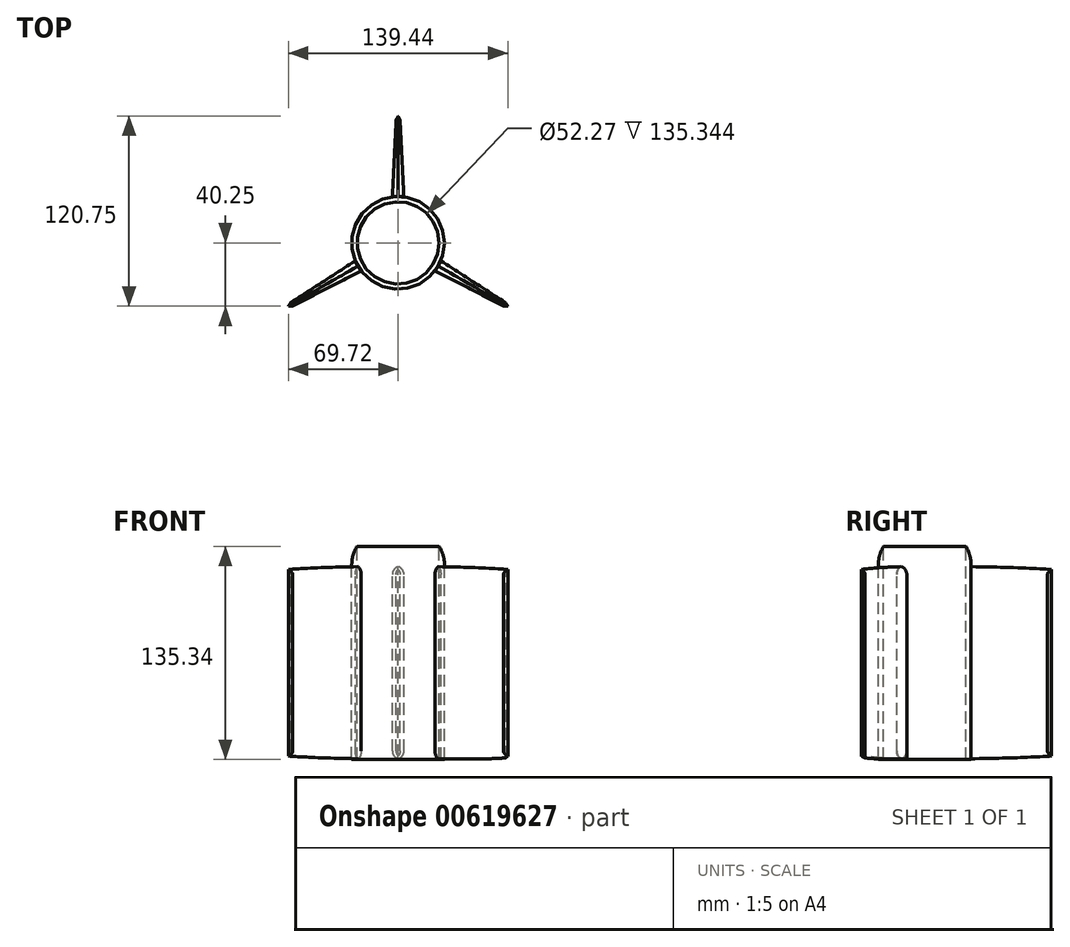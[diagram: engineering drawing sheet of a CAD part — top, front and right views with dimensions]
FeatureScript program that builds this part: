
annotation { "Feature Type Name" : "Feature", "Feature Type Description" : "" }
export const myFeature = defineFeature(function(context is Context, id is Id, definition is map)
    precondition{}
    {
        {
            var Q0;
            Q0=qCreatedBy(makeId("Front.planeOp"),FACE);
            var sketch = newSketch(context, id + "F0", { "sketchPlane" : qUnion([Q0])});
            skLineSegment(sketch, "E0.bottom", {"start": v(-26.13, 61.32) * mm, "end": v(26.13, 61.32) * mm});
            skLineSegment(sketch, "E0.top", {"start": v(-26.13, -61.32) * mm, "end": v(26.13, -61.32) * mm});
            skLineSegment(sketch, "E0.left", {"start": v(-26.13, 61.32) * mm, "end": v(-26.13, -61.32) * mm});
            skLineSegment(sketch, "E0.right", {"start": v(26.13, 61.32) * mm, "end": v(26.13, -61.32) * mm});
            skPoint(sketch, "E0.middle", {"position": v(0, 0) * mm});
            skLineSegment(sketch, "E1", {"start": v(0, 61.32) * mm, "end": v(0, -61.32) * mm});
            skLineSegment(sketch, "E2.bottom", {"start": v(-29.43, 61.32) * mm, "end": v(29.43, 61.32) * mm});
            skLineSegment(sketch, "E2.top", {"start": v(-29.43, -61.32) * mm, "end": v(29.43, -61.32) * mm});
            skLineSegment(sketch, "E2.left", {"start": v(-29.43, 61.32) * mm, "end": v(-29.43, -61.32) * mm});
            skLineSegment(sketch, "E2.right", {"start": v(29.43, 61.32) * mm, "end": v(29.43, -61.32) * mm});
            skSolve(sketch);
        }
        {
            var Q0;
            {var subQ0=sQuery(id+"F0.wireOp",EDGE,"E0.left");Q0=makeQuery(id+"F0.imprint","IMPRINT",FACE,{"disambiguationData":[TD([[makeQuery(id+"F0.imprint","IMPRINT",EDGE,{"derivedFrom":subQ0}),-1.0]])]});}
            var Q1;
            Q1=sQuery(id+"F0.wireOp",EDGE,"E1");
            revolve(context, id + "F1", {"entities" : qUnion([Q0]), "axis" : qUnion([Q1]), "revolveType" : RevolveType.FULL});
        }
        {
            var Q0;
            Q0=makeQuery(id+"F1.opRevolve","SWEPT_FACE",FACE,{"disambiguationData":[OSD([sQuery(id+"F0.wireOp",EDGE,"E2.bottom")])]});
            var sketch = newSketch(context, id + "F2", { "sketchPlane" : qUnion([Q0])});
            skLineSegment(sketch, "E3", {"start": v(0, 29.43) * mm, "end": v(0, 80.5) * mm});
            skCircle(sketch, "E4.cCircle", {"center": v(0, 0) * mm, "radius": 29.43 * mm, "construction": true});
            skLineSegment(sketch, "E5.1.0", {"start": v(-25.49, -14.72) * mm, "end": v(-69.72, -40.25) * mm});
            skLineSegment(sketch, "E5.2.0", {"start": v(25.49, -14.72) * mm, "end": v(69.72, -40.25) * mm});
            skLineSegment(sketch, "E6", {"start": v(3.68, 29.2) * mm, "end": v(1.25, 78.03) * mm});
            skLineSegment(sketch, "E7", {"start": v(1.25, 78.03) * mm, "end": v(0, 80.5) * mm});
            skLineSegment(sketch, "E8.MirrorCS", {"start": v(-3.68, 29.2) * mm, "end": v(-1.25, 78.03) * mm});
            skLineSegment(sketch, "E9.MirrorCS", {"start": v(-1.25, 78.03) * mm, "end": v(0, 80.5) * mm});
            skLineSegment(sketch, "E10.1.0", {"start": v(-27.13, -11.41) * mm, "end": v(-68.2, -37.93) * mm});
            skLineSegment(sketch, "E10.2.0", {"start": v(23.45, -17.79) * mm, "end": v(66.95, -40.1) * mm});
            skLineSegment(sketch, "E11.1.0", {"start": v(-23.45, -17.79) * mm, "end": v(-66.95, -40.1) * mm});
            skLineSegment(sketch, "E11.2.0", {"start": v(27.13, -11.41) * mm, "end": v(68.2, -37.93) * mm});
            skLineSegment(sketch, "E12.1.0", {"start": v(-68.2, -37.93) * mm, "end": v(-69.72, -40.25) * mm});
            skLineSegment(sketch, "E12.1.1", {"start": v(-66.95, -40.1) * mm, "end": v(-69.72, -40.25) * mm});
            skLineSegment(sketch, "E12.2.0", {"start": v(66.95, -40.1) * mm, "end": v(69.72, -40.25) * mm});
            skLineSegment(sketch, "E12.2.1", {"start": v(68.2, -37.93) * mm, "end": v(69.72, -40.25) * mm});
            skSolve(sketch);
        }
        {
            var Q0;
            {var subQ0=sQuery(id+"F2.wireOp",EDGE,"E3");Q0=makeQuery(id+"F2.imprint","IMPRINT",FACE,{"disambiguationData":[TD([[makeQuery(id+"F2.imprint","IMPRINT",EDGE,{"derivedFrom":subQ0}),-1.0]])]});}
            var Q1;
            {var subQ0=sQuery(id+"F2.wireOp",EDGE,"E3");Q1=makeQuery(id+"F2.imprint","IMPRINT",FACE,{"disambiguationData":[TD([[makeQuery(id+"F2.imprint","IMPRINT",EDGE,{"derivedFrom":subQ0}),1.0]])]});}
            var Q2;
            {var subQ0=sQuery(id+"F2.wireOp",EDGE,"E5.1.0");Q2=makeQuery(id+"F2.imprint","IMPRINT",FACE,{"disambiguationData":[TD([[makeQuery(id+"F2.imprint","IMPRINT",EDGE,{"derivedFrom":subQ0}),-1.0]])]});}
            var Q3;
            {var subQ0=sQuery(id+"F2.wireOp",EDGE,"E5.1.0");Q3=makeQuery(id+"F2.imprint","IMPRINT",FACE,{"disambiguationData":[TD([[makeQuery(id+"F2.imprint","IMPRINT",EDGE,{"derivedFrom":subQ0}),1.0]])]});}
            var Q4;
            {var subQ0=sQuery(id+"F2.wireOp",EDGE,"E5.2.0");Q4=makeQuery(id+"F2.imprint","IMPRINT",FACE,{"disambiguationData":[TD([[makeQuery(id+"F2.imprint","IMPRINT",EDGE,{"derivedFrom":subQ0}),-1.0]])]});}
            var Q5;
            {var subQ0=sQuery(id+"F2.wireOp",EDGE,"E5.2.0");Q5=makeQuery(id+"F2.imprint","IMPRINT",FACE,{"disambiguationData":[TD([[makeQuery(id+"F2.imprint","IMPRINT",EDGE,{"derivedFrom":subQ0}),1.0]])]});}
            extrude(context, id + "F3", {"entities" : qUnion([Q0, Q1, Q2, Q3, Q4, Q5]), "oppositeDirection" : true, "depth" : 122.43 * mm, "offsetDistance" : 25.4 * mm});
        }
        {
            var Q0;
            Q0=makeQuery(id+"F3.opExtrude","CAP_EDGE",EDGE,{"disambiguationData":[OSD([sQuery(id+"F2.wireOp",EDGE,"E8.MirrorCS")])],"isStart":true});
            var Q1;
            Q1=makeQuery(id+"F3.opExtrude","CAP_EDGE",EDGE,{"disambiguationData":[OSD([sQuery(id+"F2.wireOp",EDGE,"E11.1.0")])],"isStart":true});
            var Q2;
            Q2=makeQuery(id+"F3.opExtrude","CAP_EDGE",EDGE,{"disambiguationData":[OSD([sQuery(id+"F2.wireOp",EDGE,"E11.2.0")])],"isStart":true});
            var Q3;
            Q3=makeQuery(id+"F3.opExtrude","CAP_EDGE",EDGE,{"disambiguationData":[OSD([sQuery(id+"F2.wireOp",EDGE,"E10.1.0")])],"isStart":true});
            var Q4;
            Q4=makeQuery(id+"F3.opExtrude","CAP_EDGE",EDGE,{"disambiguationData":[OSD([sQuery(id+"F2.wireOp",EDGE,"E6")])],"isStart":true});
            var Q5;
            Q5=makeQuery(id+"F3.opExtrude","CAP_EDGE",EDGE,{"disambiguationData":[OSD([sQuery(id+"F2.wireOp",EDGE,"E10.2.0")])],"isStart":true});
            fillet(context, id + "F4", {"entities" : qUnion([Q0, Q1, Q2, Q3, Q4, Q5]), "radius" : 5.08 * mm, "tangentPropagation" : true, "rho" : .4, "crossSection" : FilletCrossSection.CONIC, "allowEdgeOverflow" : false});
        }
        {
            var Q0;
            Q0=makeQuery(id+"F3.opExtrude","CAP_EDGE",EDGE,{"disambiguationData":[OSD([sQuery(id+"F2.wireOp",EDGE,"E10.2.0")])],"isStart":false});
            var Q1;
            Q1=makeQuery(id+"F3.opExtrude","CAP_EDGE",EDGE,{"disambiguationData":[OSD([sQuery(id+"F2.wireOp",EDGE,"E8.MirrorCS")])],"isStart":false});
            var Q2;
            Q2=makeQuery(id+"F3.opExtrude","CAP_EDGE",EDGE,{"disambiguationData":[OSD([sQuery(id+"F2.wireOp",EDGE,"E6")])],"isStart":false});
            var Q3;
            Q3=makeQuery(id+"F3.opExtrude","CAP_EDGE",EDGE,{"disambiguationData":[OSD([sQuery(id+"F2.wireOp",EDGE,"E10.1.0")])],"isStart":false});
            var Q4;
            Q4=makeQuery(id+"F3.opExtrude","CAP_EDGE",EDGE,{"disambiguationData":[OSD([sQuery(id+"F2.wireOp",EDGE,"E11.1.0")])],"isStart":false});
            fillet(context, id + "F5", {"entities" : qUnion([Q0, Q1, Q2, Q3, Q4]), "radius" : 5.08 * mm, "tangentPropagation" : true, "allowEdgeOverflow" : false});
        }
        {
            var Q0;
            {var subQ0=sQuery(id+"F0.wireOp",EDGE,"E2.bottom");Q0=makeQuery(id+"F2.imprint","IMPRINT",FACE,{"disambiguationData":[TD([[makeQuery(id+"F2.imprint","IMPRINT",EDGE,{"derivedFrom":makeQuery(id+"F1.opRevolve","SWEPT_EDGE",EDGE,{"disambiguationData":[OSD([sQuery(id+"F0.wireOp",EDGE,"E0.left"),subQ0])]})}),-1.0]])]});}
            extrude(context, id + "F6", {"entities" : qUnion([Q0]), "operationType" : NewBodyOperationType.ADD, "depth" : 12.7 * mm, "offsetDistance" : 25.4 * mm});
        }
        {
            var Q0;
            Q0=makeQuery(id+"F6.opExtrude","CAP_EDGE",EDGE,{"disambiguationData":[OSD([sQuery(id+"F0.wireOp",EDGE,"E2.bottom"),sQuery(id+"F0.wireOp",EDGE,"E2.left")])],"isStart":false});
            fillet(context, id + "F7", {"entities" : qUnion([Q0]), "radius" : 22.86 * mm, "tangentPropagation" : true, "rho" : .5, "crossSection" : FilletCrossSection.CONIC, "allowEdgeOverflow" : false});
        }
    });
